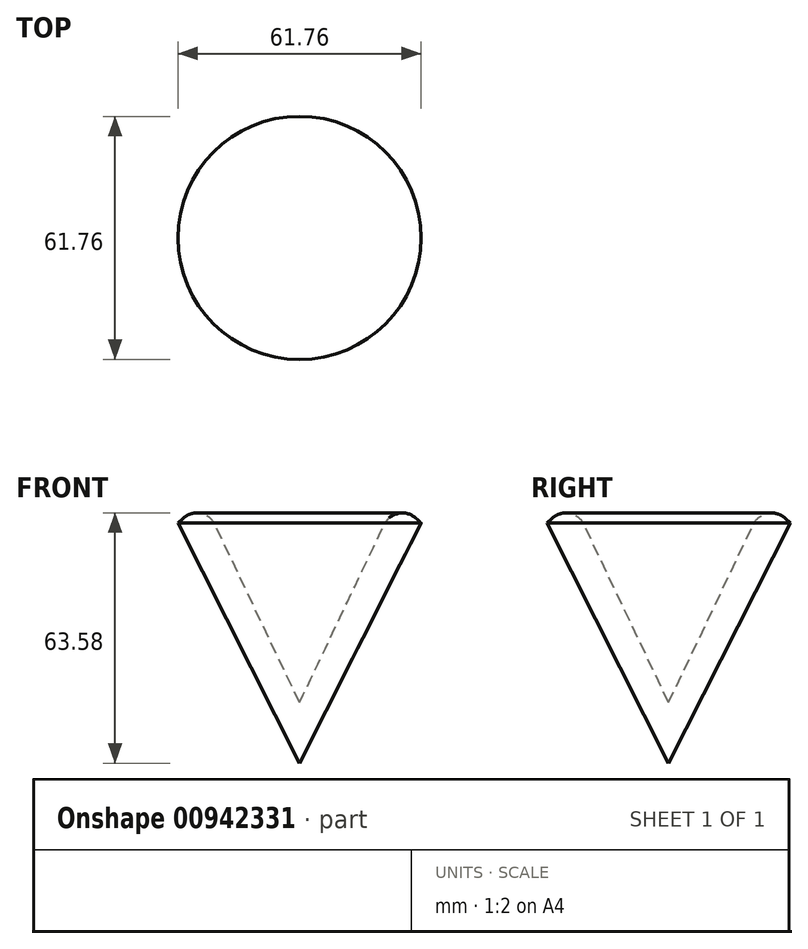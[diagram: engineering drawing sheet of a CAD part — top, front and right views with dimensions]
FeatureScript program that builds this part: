
annotation { "Feature Type Name" : "Feature", "Feature Type Description" : "" }
export const myFeature = defineFeature(function(context is Context, id is Id, definition is map)
    precondition{}
    {
        {
            var Q0;
            Q0=qCreatedBy(makeId("Front.planeOp"),FACE);
            var sketch = newSketch(context, id + "F0", { "sketchPlane" : qUnion([Q0])});
            skLineSegment(sketch, "E0", {"start": v(0, 0) * mm, "end": v(24.45, 51.43) * mm});
            skLineSegment(sketch, "E1", {"start": v(24.45, 51.43) * mm, "end": v(30.88, 45.69) * mm});
            skLineSegment(sketch, "E2", {"start": v(30.88, 45.69) * mm, "end": v(0, -15.38) * mm});
            skLineSegment(sketch, "E3", {"start": v(0, -15.38) * mm, "end": v(0, 0) * mm});
            skSolve(sketch);
        }
        {
            var Q0;
            Q0=makeQuery(id+"F0.imprint","IMPRINT",FACE,{"disambiguationData":[TD([[makeQuery(id+"F0.imprint","IMPRINT",EDGE,{"derivedFrom":sQuery(id+"F0.wireOp",EDGE,"E0")}),-1.0]])]});
            var Q1;
            Q1=sQuery(id+"F0.wireOp",EDGE,"E3");
            revolve(context, id + "F1", {"surfaceOperationType" : NewSurfaceOperationType.NEW, "entities" : qUnion([Q0]), "axis" : qUnion([Q1]), "revolveType" : RevolveType.FULL});
        }
        {
            var Q0;
            Q0=makeQuery(id+"F1.opRevolve","SWEPT_EDGE",EDGE,{"disambiguationData":[OSD([sQuery(id+"F0.wireOp",EDGE,"E0"),sQuery(id+"F0.wireOp",EDGE,"E1")])]});
            fillet(context, id + "F2", {"entities" : qUnion([Q0]), "radius" : 5.08 * mm, "tangentPropagation" : true, "allowEdgeOverflow" : false});
        }
    });
